# Revit family: Sh-2003-14-44s
name_source: partatom
category: Lighting Fixtures
revit_build: Autodesk Revit 2017 (Build: 20160225_1515(x64)
units: mm (PartAtom-declared; Revit-internal decimal feet)

## family parameters
Always vertical = Yes
Cut with Voids When Loaded = No
Light Source = No
OmniClass Number = 23.80.70.00
OmniClass Title = Lighting
Part Type = Normal
Room Calculation Point = No
Round Connector Dimension = Use Diameter
Shared = No
Work Plane-Based = No

## types (2) — shared parameters
Body Material = Aluminium
Body color = Black
Cutting Diameter = 8.0 cm
Diameter = 11.0 cm
Height = 14.3 cm
IP = IP66
Lamp = GU10
Manufacturer = SHOA
Model = SH-2003-14-44S
Protection Class = Class I
Type medule = SMD
URL = https://www.shoaco.com
Voltage/Frequency = 230V-50HZ
color rendering index(CRI) = 80
consumption current = 0 A
instalation = inground
wattage. = 7 W
website = www.shoaco.com

## per-type parameters (varying)
| type | Flicker | color temperature |
| SH-2003-14-44s(Black body-3000K-GU10) | Free flicker | 3000K |
| SH-2003-14-44s(Black body-6500K-GU10) | FREE Flicker | 6500K |

## geometry (parser evidence)
native form markers: Sweep x3
no freeform markers — native parametric forms only
